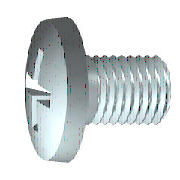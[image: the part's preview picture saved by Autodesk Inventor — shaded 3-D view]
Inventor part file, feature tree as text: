
AUTODESK INVENTOR PART (.ipt)
format: ipt  version: 2021 (Build 250183000, 183)  size: 248,832 bytes
history: native  units: mm (DEFAULTED — no unit token found)
features: chamfer x4, other x3, sketch x2, revolve x1, fillet x1, extrude x1, pattern_circular x1
ambient origin geometry x8: Origin, YZ Plane, XZ Plane, XY Plane, X Axis, Y Axis, Z Axis, Center Point
bodies: Solid1 (feature_tree)
feature tree (13):
  revolve  "Revolution1"  [1 undecoded]
  chamfer  "Chamfer1"  Distance=0.125mm
  chamfer  "Chamfer2"  Distance=0.125mm
  fillet  "Fillet1"  Radius=0.25mm
  extrude  "Extrusion1"  Depth=10.0mm
  pattern_circular  "PolarArray1"  [2 undecoded]
  chamfer  "Chamfer3"  Distance=1.612mm
  chamfer  "Chamfer4"  Distance=0.62mm
  other  "MSC_A1"
  other  "MSC_PF1"
  other  "MSC_PT1"
  sketch  "Sketch2"  dims[d6=2.75mm d9=0.872665mm]
  sketch  "Sketch3"  dims[d10=90.0deg d11=0.125mm d12=0.125mm d13=0.25mm d14=0.25mm d16=10.0mm d17=0.0mm d19=1.612mm d20=0.62mm d21=2.52mm d22=0.516667mm d23=0.0mm d24=40.0mm d26=360.0deg d28=0.0mm d29=0.0mm d30=0.442857mm d31=0.442857mm d32=0.206667mm d33=0.206667mm d34=45.0deg d35=45.0deg d36=45.0deg d37=45.0deg d38=0.0mm d39=0.0mm d40=0.0mm]
note: 3 required parameter values undecoded (feature->parameter linkage not recoverable at this tier; creation-order binding heuristic only, values carry confidence <= 0.55)